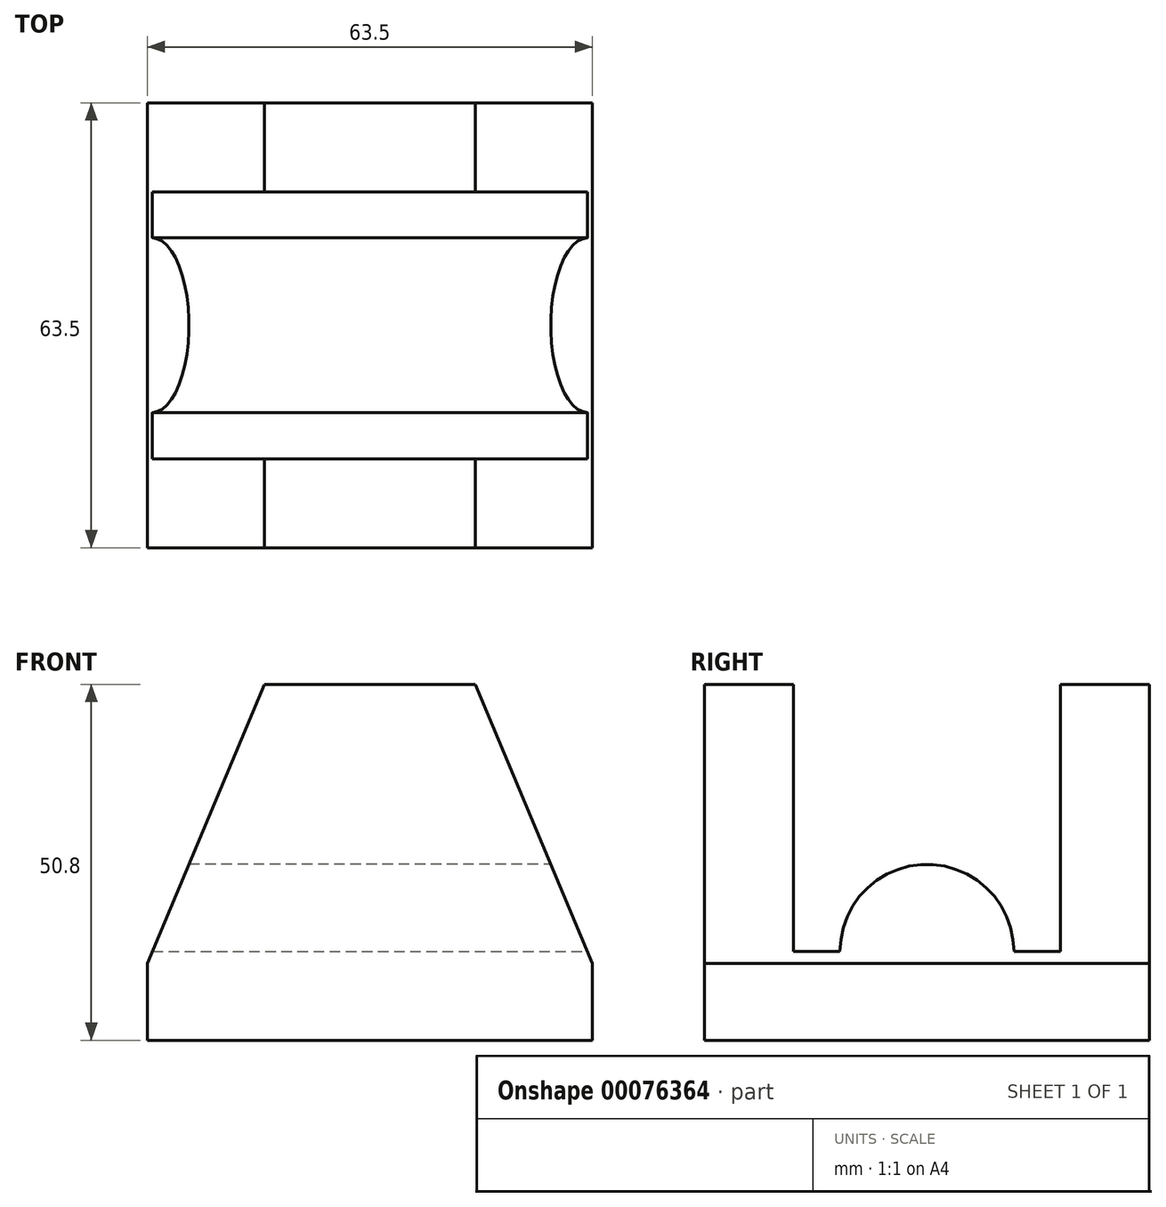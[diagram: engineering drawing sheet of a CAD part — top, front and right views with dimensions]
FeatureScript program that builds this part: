
annotation { "Feature Type Name" : "Feature", "Feature Type Description" : "" }
export const myFeature = defineFeature(function(context is Context, id is Id, definition is map)
    precondition{}
    {
        {
            var Q0;
            Q0=qCreatedBy(makeId("Top.planeOp"),FACE);
            var sketch = newSketch(context, id + "F0", { "sketchPlane" : qUnion([Q0])});
            skLineSegment(sketch, "E0.rect.bottom", {"start": v(31.75, 31.75) * mm, "end": v(-31.75, 31.75) * mm});
            skLineSegment(sketch, "E0.rect.top", {"start": v(31.75, -31.75) * mm, "end": v(-31.75, -31.75) * mm});
            skLineSegment(sketch, "E0.rect.left", {"start": v(31.75, 31.75) * mm, "end": v(31.75, -31.75) * mm});
            skLineSegment(sketch, "E0.rect.right", {"start": v(-31.75, 31.75) * mm, "end": v(-31.75, -31.75) * mm});
            skPoint(sketch, "E0.rect.middle", {"position": v(0, 0) * mm});
            skSolve(sketch);
        }
        {
            var Q0;
            Q0=makeQuery(id+"F0.imprint","IMPRINT",FACE,{"disambiguationData":[TD([[makeQuery(id+"F0.imprint","IMPRINT",EDGE,{"derivedFrom":sQuery(id+"F0.wireOp",EDGE,"E0.rect.bottom")}),1.0]])]});
            extrude(context, id + "F1", {"entities" : qUnion([Q0]), "depth" : 12.7 * mm});
        }
        {
            var Q0;
            Q0=makeQuery(id+"F1.opExtrude","SWEPT_FACE",FACE,{"disambiguationData":[OSD([sQuery(id+"F0.wireOp",EDGE,"E0.rect.right")])]});
            var sketch = newSketch(context, id + "F2", { "sketchPlane" : qUnion([Q0])});
            skLineSegment(sketch, "E1.bottom", {"start": v(-31.75, 12.7) * mm, "end": v(-19.05, 12.7) * mm});
            skLineSegment(sketch, "E1.top", {"start": v(-31.75, 50.8) * mm, "end": v(-19.05, 50.8) * mm});
            skLineSegment(sketch, "E1.left", {"start": v(-31.75, 12.7) * mm, "end": v(-31.75, 50.8) * mm});
            skLineSegment(sketch, "E1.right", {"start": v(-19.05, 12.7) * mm, "end": v(-19.05, 50.8) * mm});
            skLineSegment(sketch, "E2.MirrorCS", {"start": v(19.05, 12.7) * mm, "end": v(19.05, 50.8) * mm});
            skLineSegment(sketch, "E3.MirrorCS", {"start": v(31.75, 12.7) * mm, "end": v(31.75, 50.8) * mm});
            skLineSegment(sketch, "E4.MirrorCS", {"start": v(31.75, 50.8) * mm, "end": v(19.05, 50.8) * mm});
            skLineSegment(sketch, "E5.MirrorCS", {"start": v(31.75, 12.7) * mm, "end": v(19.05, 12.7) * mm});
            skSolve(sketch);
        }
        {
            var Q0;
            Q0=qSketchRegion(id+"F2",true);
            extrude(context, id + "F3", {"entities" : qUnion([Q0]), "operationType" : NewBodyOperationType.ADD, "oppositeDirection" : true, "depth" : 63.5 * mm});
        }
        {
            var Q0;
            Q0=makeQuery(id+"F3.boolean.opBoolean","MERGE",FACE,{"derivedFrom":[makeQuery(id+"F1.opExtrude","SWEPT_FACE",FACE,{"disambiguationData":[OSD([sQuery(id+"F0.wireOp",EDGE,"E0.rect.left")])]}),makeQuery(id+"F3.opExtrude","CAP_FACE",FACE,{"disambiguationData":[OSD([sQuery(id+"F2.wireOp",EDGE,"E1.bottom"),sQuery(id+"F2.wireOp",EDGE,"E1.top"),sQuery(id+"F2.wireOp",EDGE,"E1.left"),sQuery(id+"F2.wireOp",EDGE,"E1.right")])],"isStart":false}),makeQuery(id+"F3.opExtrude","CAP_FACE",FACE,{"disambiguationData":[OSD([sQuery(id+"F2.wireOp",EDGE,"E2.MirrorCS"),sQuery(id+"F2.wireOp",EDGE,"E3.MirrorCS"),sQuery(id+"F2.wireOp",EDGE,"E4.MirrorCS"),sQuery(id+"F2.wireOp",EDGE,"E5.MirrorCS")])],"isStart":false})]});
            var sketch = newSketch(context, id + "F4", { "sketchPlane" : qUnion([Q0])});
            skCircle(sketch, "E6", {"center": v(0, 12.72) * mm, "radius": 12.46 * mm});
            skSolve(sketch);
        }
        {
            var Q0;
            Q0=qSketchRegion(id+"F4",true);
            extrude(context, id + "F5", {"entities" : qUnion([Q0]), "operationType" : NewBodyOperationType.ADD, "oppositeDirection" : true, "depth" : 63.5 * mm});
        }
        {
            var Q0;
            Q0=makeQuery(id+"F3.boolean.opBoolean","MERGE",FACE,{"derivedFrom":[makeQuery(id+"F1.opExtrude","SWEPT_FACE",FACE,{"disambiguationData":[OSD([sQuery(id+"F0.wireOp",EDGE,"E0.rect.bottom")])]}),makeQuery(id+"F3.opExtrude","SWEPT_FACE",FACE,{"disambiguationData":[OSD([sQuery(id+"F2.wireOp",EDGE,"E1.left")])]})]});
            var sketch = newSketch(context, id + "F6", { "sketchPlane" : qUnion([Q0])});
            skLineSegment(sketch, "E7", {"start": v(-31.75, 10.99) * mm, "end": v(-15.04, 50.8) * mm});
            skLineSegment(sketch, "E8", {"start": v(-15.04, 50.8) * mm, "end": v(-31.75, 50.8) * mm});
            skLineSegment(sketch, "E9", {"start": v(-31.75, 50.8) * mm, "end": v(-31.75, 10.99) * mm});
            skLineSegment(sketch, "E10.MirrorCS", {"start": v(31.75, 10.99) * mm, "end": v(15.04, 50.8) * mm});
            skLineSegment(sketch, "E11.MirrorCS", {"start": v(15.04, 50.8) * mm, "end": v(31.75, 50.8) * mm});
            skLineSegment(sketch, "E12.MirrorCS", {"start": v(31.75, 50.8) * mm, "end": v(31.75, 10.99) * mm});
            skSolve(sketch);
        }
        {
            var Q0;
            Q0=qSketchRegion(id+"F6",true);
            extrude(context, id + "F7", {"entities" : qUnion([Q0]), "operationType" : NewBodyOperationType.REMOVE, "oppositeDirection" : true, "depth" : 63.5 * mm});
        }
    });
